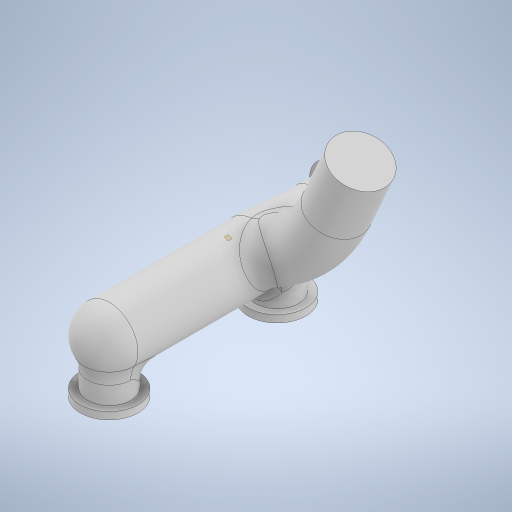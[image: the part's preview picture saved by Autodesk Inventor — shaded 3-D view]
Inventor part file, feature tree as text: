
AUTODESK INVENTOR PART (.ipt)
format: ipt  version: 2023 (Build 270158000, 158)  size: 776,192 bytes
history: native  units: in
note: dims shown in document units (in); Inventor stores cm internally (conversion verified against a paired STEP export)
features: sketch x7, extrude x5, plane x3, fillet x3, revolve x1, loft x1, sweep x1, mirror x1, other x1, projected_geometry x1
ambient origin geometry x8: Origin, YZ Plane, XZ Plane, XY Plane, X Axis, Y Axis, Z Axis, Center Point
bodies: Solid1 (feature_tree)
feature tree (24):
  revolve  "Revolution1"  [1 undecoded]
  plane  "Work Plane1"
  loft  "Loft1"
  extrude  "Extrusion1"  Depth=2.0in
  fillet  "Fillet1"  Radius=0.3937in
  extrude  "Extrusion2"  Depth=9.0in
  extrude  "Extrusion3"  Depth=11.0in TaperAngle=0.0deg
  extrude  "Extrusion4"  Depth=12.0in
  plane  "Work Plane3"
  sketch  "Sketch9"  dims[d20=12.0in d21=12.0in]
  plane  "Work Plane2"
  sweep  "Sweep2"
  fillet  "Fillet5"  Radius=1.0in
  extrude  "Extrusion6"  Depth=8.0in
  mirror  "Mirror3"
  fillet  "Fillet7"  Radius=5.25in
  sketch  "Sketch3"  dims[d3=30.0in d4=6.0in]
  other  "Edges1"
  sketch  "Sketch4"  dims[d5=90.0deg d6=12.0in]
  sketch  "Sketch5"  dims[d7=8.0in d8=2.0in d9=0.3937in d10=90.0deg]
  projected_geometry  "Projected Loop1"
  sketch  "Sketch6"  dims[d13=0.3937in d14=90.0deg d15=9.0in]
  sketch  "Sketch7"  dims[d16=9.0in d17=11.0in d18=0.0in]
  sketch  "Sketch10"  dims[d22=1.5in d23=0.0in d24=6.0in d25=6.0in d26=6.0in d27=0.0in d28=2.0in d29=0.1969in d30=6.0in d31=0.3937in d33=1.0in d34=0.0in d35=8.0in d36=5.25in d37=0.0in d52=11.0in d56=0.0in d57=0.0in d58=3.0in d59=0.0in d60=5.0in d61=11.0in d62=1.5in d63=0.0in d74=2.5in d75=13.78in d76=3.0in]
note: 1 required parameter value undecoded (feature->parameter linkage not recoverable at this tier; creation-order binding heuristic only, values carry confidence <= 0.55)
